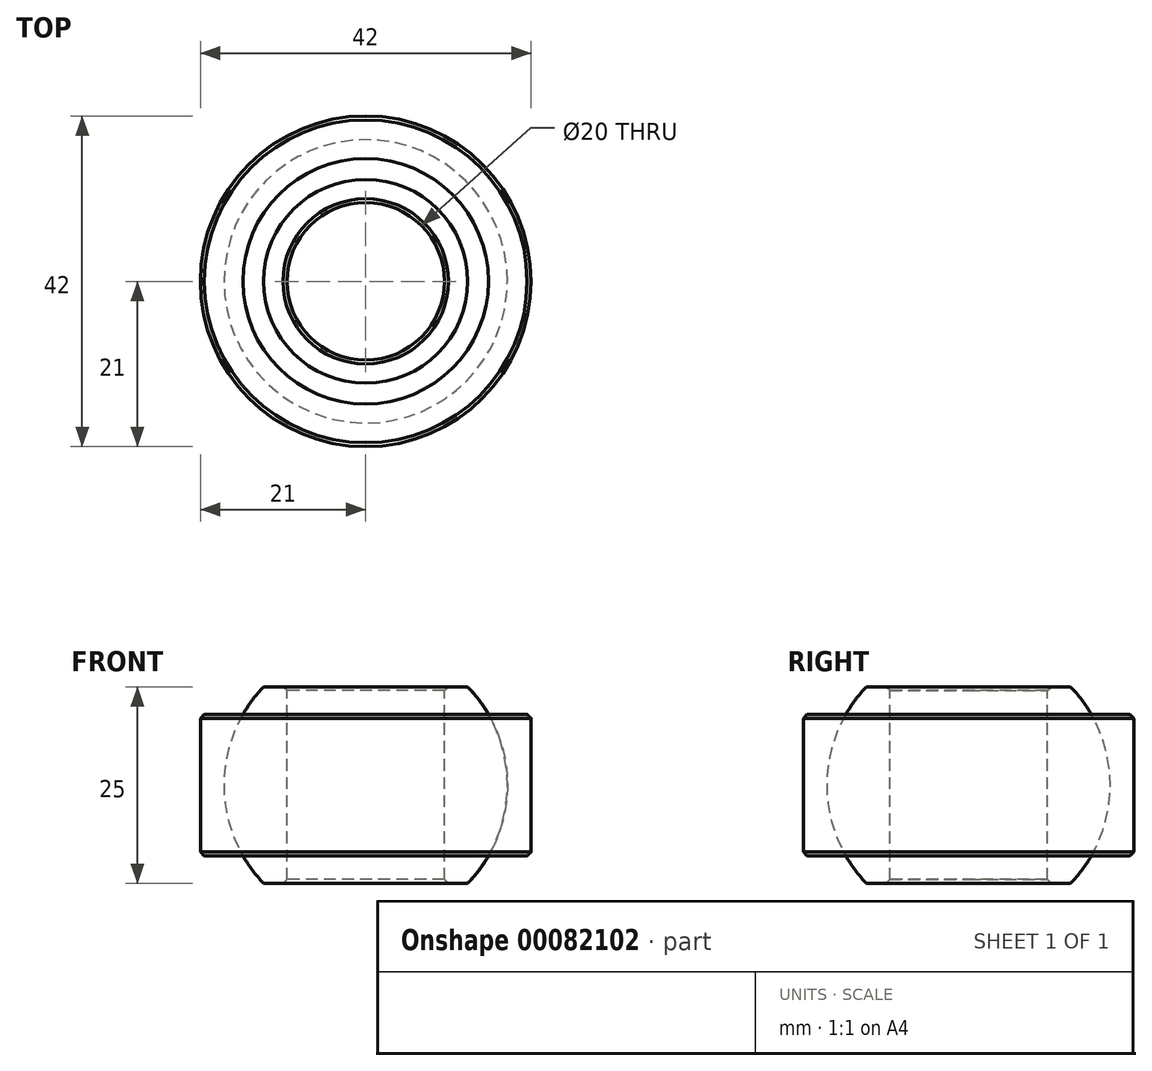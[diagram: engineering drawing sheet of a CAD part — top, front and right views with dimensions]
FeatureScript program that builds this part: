
annotation { "Feature Type Name" : "Feature", "Feature Type Description" : "" }
export const myFeature = defineFeature(function(context is Context, id is Id, definition is map)
    precondition{}
    {
        {
            var Q0;
            Q0=qCreatedBy(makeId("Top.planeOp"),FACE);
            var sketch = newSketch(context, id + "F0", { "sketchPlane" : qUnion([Q0])});
            skCircle(sketch, "E0", {"center": v(0, 0) * mm, "radius": 21 * mm});
            skSolve(sketch);
        }
        {
            var Q0;
            Q0 = qSketchRegion(id + "F0", true);
            extrude(context, id + "F1", {"entities" : qUnion([Q0]), "depth" : 18 * mm, "symmetric" : true});
        }
        {
            var Q0;
            Q0=qCreatedBy(makeId("Front.planeOp"),FACE);
            var sketch = newSketch(context, id + "F2", { "sketchPlane" : qUnion([Q0])});
            skCircle(sketch, "E1", {"center": v(0, 0) * mm, "radius": 18 * mm});
            skLineSegment(sketch, "E2", {"start": v(0, -25.67) * mm, "end": v(0, 27.5) * mm});
            skSolve(sketch);
        }
        {
            var Q0;
            {var subQ0=sQuery(id+"F2.wireOp",EDGE,"E2");var subQ1=sQuery(id+"F2.wireOp",EDGE,"E1");var subQ2=makeQuery(id+"F2.imprint","INTERSECT",VERTEX,{"disambiguationData":[OD(0.0)],"derivedFrom":[subQ1,subQ0]});Q0=makeQuery(id+"F2.imprint","IMPRINT",FACE,{"disambiguationData":[TD([[makeQuery(id+"F2.imprint","IMPRINT",EDGE,{"disambiguationData":[TD([[subQ2,-1.0]])],"derivedFrom":subQ1}),1.0]])]});}
            var Q1;
            Q1=sQuery(id+"F2.wireOp",EDGE,"E2");
            revolve(context, id + "F3", {"operationType" : NewBodyOperationType.REMOVE, "entities" : qUnion([Q0]), "axis" : qUnion([Q1]), "revolveType" : RevolveType.FULL, "oppositeDirection" : true});
        }
        {
            var Q0;
            {var subQ0=sQuery(id+"F2.wireOp",EDGE,"E2");var subQ1=sQuery(id+"F2.wireOp",EDGE,"E1");var subQ2=makeQuery(id+"F2.imprint","INTERSECT",VERTEX,{"disambiguationData":[OD(0.0)],"derivedFrom":[subQ1,subQ0]});Q0=makeQuery(id+"F2.imprint","IMPRINT",FACE,{"disambiguationData":[TD([[makeQuery(id+"F2.imprint","IMPRINT",EDGE,{"disambiguationData":[TD([[subQ2,-1.0]])],"derivedFrom":subQ1}),1.0]])]});}
            var Q1;
            Q1=sQuery(id+"F2.wireOp",EDGE,"E2");
            revolve(context, id + "F4", {"entities" : qUnion([Q0]), "axis" : qUnion([Q1]), "revolveType" : RevolveType.FULL});
        }
        {
            var Q0;
            Q0=qCreatedBy(makeId("Front.planeOp"),FACE);
            var sketch = newSketch(context, id + "F5", { "sketchPlane" : qUnion([Q0])});
            skLineSegment(sketch, "E3.bottom", {"start": v(34.68, 12.5) * mm, "end": v(-34.68, 12.5) * mm});
            skLineSegment(sketch, "E3.top", {"start": v(34.68, 49.29) * mm, "end": v(-34.68, 49.29) * mm});
            skLineSegment(sketch, "E3.left", {"start": v(34.68, 12.5) * mm, "end": v(34.68, 49.29) * mm});
            skLineSegment(sketch, "E3.right", {"start": v(-34.68, 12.5) * mm, "end": v(-34.68, 49.29) * mm});
            skPoint(sketch, "E3.middle", {"position": v(0, 30.9) * mm});
            skLineSegment(sketch, "E4.bottom", {"start": v(41.3, -37.03) * mm, "end": v(-41.3, -37.03) * mm});
            skLineSegment(sketch, "E4.top", {"start": v(41.3, -12.5) * mm, "end": v(-41.3, -12.5) * mm});
            skLineSegment(sketch, "E4.left", {"start": v(41.3, -37.03) * mm, "end": v(41.3, -12.5) * mm});
            skLineSegment(sketch, "E4.right", {"start": v(-41.3, -37.03) * mm, "end": v(-41.3, -12.5) * mm});
            skPoint(sketch, "E4.middle", {"position": v(0, -24.76) * mm});
            skSolve(sketch);
        }
        {
            var Q0;
            Q0 = qSketchRegion(id + "F5", true);
            extrude(context, id + "F6", {"entities" : qUnion([Q0]), "operationType" : NewBodyOperationType.REMOVE, "endBound" : BoundingType.THROUGH_ALL, "oppositeDirection" : true, "depth" : 25 * mm, "hasSecondDirection" : true, "secondDirectionBound" : BoundingType.THROUGH_ALL, "secondDirectionOppositeDirection" : false, "secondDirectionDepth" : 25 * mm});
        }
        {
            var Q0;
            Q0=makeQuery(id+"F6.boolean.opBoolean","COPY",FACE,{"derivedFrom":makeQuery(id+"F6.opExtrude","SWEPT_FACE",FACE,{"disambiguationData":[OSD([sQuery(id+"F5.wireOp",EDGE,"E3.bottom")])]})});
            var sketch = newSketch(context, id + "F7", { "sketchPlane" : qUnion([Q0])});
            skCircle(sketch, "E5", {"center": v(0, 0) * mm, "radius": 10 * mm});
            skSolve(sketch);
        }
        {
            var Q0;
            Q0 = qSketchRegion(id + "F7", true);
            extrude(context, id + "F8", {"entities" : qUnion([Q0]), "operationType" : NewBodyOperationType.REMOVE, "endBound" : BoundingType.THROUGH_ALL, "oppositeDirection" : true, "depth" : 25 * mm});
        }
        {
            var Q0;
            Q0=makeQuery(id+"F1.opExtrude","CAP_EDGE",EDGE,{"disambiguationData":[OSD([sQuery(id+"F0.wireOp",EDGE,"E0")])],"isStart":false});
            var Q1;
            Q1=makeQuery(id+"F8.boolean.opBoolean","COPY",FACE,{"derivedFrom":makeQuery(id+"F8.opExtrude","SWEPT_FACE",FACE,{"disambiguationData":[OSD([sQuery(id+"F7.wireOp",EDGE,"E5")])]})});
            var Q2;
            Q2=makeQuery(id+"F1.opExtrude","CAP_EDGE",EDGE,{"disambiguationData":[OSD([sQuery(id+"F0.wireOp",EDGE,"E0")])],"isStart":true});
            chamfer(context, id + "F9", {"entities" : qUnion([Q0, Q1, Q2]), "width" : 0.5 * mm, "tangentPropagation" : true});
        }
    });
